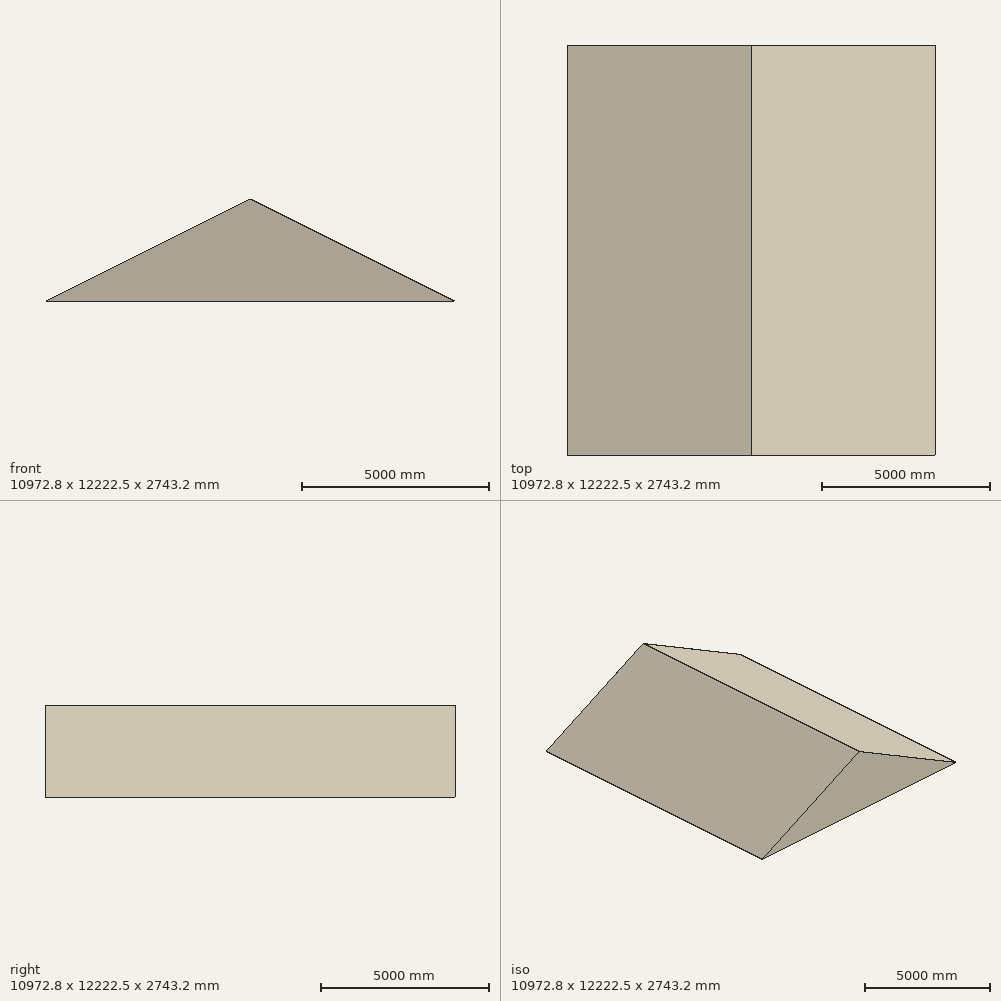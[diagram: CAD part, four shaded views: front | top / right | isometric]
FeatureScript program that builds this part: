
annotation { "Feature Type Name" : "Feature", "Feature Type Description" : "" }
export const myFeature = defineFeature(function(context is Context, id is Id, definition is map)
    precondition{}
    {
        {
            var Q0;
            Q0=qCreatedBy(makeId("Front.planeOp"),FACE);
            var sketch = newSketch(context, id + "F0", { "sketchPlane" : qUnion([Q0])});
            skLineSegment(sketch, "E0", {"start": v(0, 0) * mm, "end": v(-4572, 0) * mm});
            skLineSegment(sketch, "E1", {"start": v(0, 0) * mm, "end": v(4572, 0) * mm});
            skLineSegment(sketch, "E2", {"start": v(-4572, 0) * mm, "end": v(-4572, 3352.8) * mm});
            skLineSegment(sketch, "E3", {"start": v(4572, 0) * mm, "end": v(4572, 3352.8) * mm});
            skLineSegment(sketch, "E4", {"start": v(0, 0) * mm, "end": v(0, 3352.8) * mm, "construction": true});
            skLineSegment(sketch, "E5", {"start": v(4572, 3352.8) * mm, "end": v(0, 3352.8) * mm});
            skLineSegment(sketch, "E6", {"start": v(-4572, 3352.8) * mm, "end": v(0, 3352.8) * mm});
            skLineSegment(sketch, "E7", {"start": v(0, 3352.8) * mm, "end": v(0, 5638.8) * mm, "construction": true});
            skLineSegment(sketch, "E8", {"start": v(0, 5638.8) * mm, "end": v(4572, 3352.8) * mm});
            skLineSegment(sketch, "E9", {"start": v(0, 5638.8) * mm, "end": v(-4572, 3352.8) * mm});
            skLineSegment(sketch, "E10", {"start": v(4572, 3352.8) * mm, "end": v(5486.4, 3352.8) * mm});
            skLineSegment(sketch, "E11", {"start": v(-4572, 3352.8) * mm, "end": v(-5486.4, 3352.8) * mm});
            skLineSegment(sketch, "E12", {"start": v(0, 5638.8) * mm, "end": v(0, 6096) * mm});
            skLineSegment(sketch, "E13", {"start": v(0, 6096) * mm, "end": v(5486.4, 3352.8) * mm});
            skLineSegment(sketch, "E14", {"start": v(0, 6096) * mm, "end": v(-5486.4, 3352.8) * mm});
            skPoint(sketch, "E15.endSnap0", {"position": v(-5029.2, 3352.8) * mm});
            skLineSegment(sketch, "E16", {"start": v(-4572, 0) * mm, "end": v(-4572, -609.6) * mm});
            skLineSegment(sketch, "E17", {"start": v(-4572, -609.6) * mm, "end": v(4572, -609.6) * mm});
            skLineSegment(sketch, "E18", {"start": v(4572, 0) * mm, "end": v(4572, -609.6) * mm});
            skLineSegment(sketch, "E19", {"start": v(4572, 3352.8) * mm, "end": v(9143.16, 2743.2) * mm});
            skLineSegment(sketch, "E20", {"start": v(4572, 0) * mm, "end": v(9144, 0) * mm});
            skLineSegment(sketch, "E21", {"start": v(9144, 0) * mm, "end": v(9143.16, 2743.2) * mm});
            skLineSegment(sketch, "E22.bottom", {"start": v(609.6, 1981.2) * mm, "end": v(3352.8, 1981.2) * mm});
            skLineSegment(sketch, "E22.top", {"start": v(609.6, 609.6) * mm, "end": v(3352.8, 609.6) * mm});
            skLineSegment(sketch, "E22.left", {"start": v(609.6, 1981.2) * mm, "end": v(609.6, 609.6) * mm});
            skLineSegment(sketch, "E22.right", {"start": v(3352.8, 1981.2) * mm, "end": v(3352.8, 609.6) * mm});
            skLineSegment(sketch, "E23", {"start": v(4572, -609.6) * mm, "end": v(9144, -609.6) * mm});
            skLineSegment(sketch, "E24", {"start": v(9144, 0) * mm, "end": v(9144, -609.6) * mm});
            skLineSegment(sketch, "E25.0", {"start": v(762, 1828.8) * mm, "end": v(3200.4, 1828.8) * mm});
            skLineSegment(sketch, "E25.1", {"start": v(762, 1828.8) * mm, "end": v(762, 762) * mm});
            skLineSegment(sketch, "E25.2", {"start": v(762, 762) * mm, "end": v(3200.4, 762) * mm});
            skLineSegment(sketch, "E25.3", {"start": v(3200.4, 1828.8) * mm, "end": v(3200.4, 762) * mm});
            skLineSegment(sketch, "E26.bottom", {"start": v(7315.2, 609.6) * mm, "end": v(6096, 609.6) * mm});
            skLineSegment(sketch, "E26.top", {"start": v(7315.2, 1981.2) * mm, "end": v(6096, 1981.2) * mm});
            skLineSegment(sketch, "E26.left", {"start": v(7315.2, 609.6) * mm, "end": v(7315.2, 1981.2) * mm});
            skLineSegment(sketch, "E26.right", {"start": v(6096, 609.6) * mm, "end": v(6096, 1981.2) * mm});
            skLineSegment(sketch, "E27.0", {"start": v(6248.4, 762) * mm, "end": v(6248.4, 1828.8) * mm});
            skLineSegment(sketch, "E27.1", {"start": v(7162.8, 762) * mm, "end": v(6248.4, 762) * mm});
            skLineSegment(sketch, "E27.2", {"start": v(7162.8, 762) * mm, "end": v(7162.8, 1828.8) * mm});
            skLineSegment(sketch, "E27.3", {"start": v(7162.8, 1828.8) * mm, "end": v(6248.4, 1828.8) * mm});
            skLineSegment(sketch, "E28.bottom", {"start": v(-2438.4, 0) * mm, "end": v(-3352.8, 0) * mm});
            skLineSegment(sketch, "E28.top", {"start": v(-2438.4, 2133.6) * mm, "end": v(-3352.8, 2133.6) * mm});
            skLineSegment(sketch, "E28.left", {"start": v(-2438.4, 0) * mm, "end": v(-2438.4, 2133.6) * mm});
            skLineSegment(sketch, "E28.right", {"start": v(-3352.8, 0) * mm, "end": v(-3352.8, 2133.6) * mm});
            skLineSegment(sketch, "E29", {"start": v(4572, 2743.2) * mm, "end": v(9143.34, 2133.57) * mm});
            skLineSegment(sketch, "E30.bottom", {"start": v(-3200.4, 1981.2) * mm, "end": v(-2590.8, 1981.2) * mm});
            skLineSegment(sketch, "E30.top", {"start": v(-3200.4, 0) * mm, "end": v(-2590.8, 0) * mm});
            skLineSegment(sketch, "E30.left", {"start": v(-3200.4, 1981.2) * mm, "end": v(-3200.4, 0) * mm});
            skLineSegment(sketch, "E30.right", {"start": v(-2590.8, 1981.2) * mm, "end": v(-2590.8, 0) * mm});
            skSolve(sketch);
        }
        {
            var Q0;
            Q0=makeQuery(id+"F0.imprint","IMPRINT",FACE,{"disambiguationData":[TD([[makeQuery(id+"F0.imprint","IMPRINT",EDGE,{"derivedFrom":sQuery(id+"F0.wireOp",EDGE,"E9")}),-1.0]])]});
            var Q1;
            Q1=makeQuery(id+"F0.imprint","IMPRINT",FACE,{"disambiguationData":[TD([[makeQuery(id+"F0.imprint","IMPRINT",EDGE,{"derivedFrom":sQuery(id+"F0.wireOp",EDGE,"E8")}),1.0]])]});
            extrude(context, id + "F1", {"entities" : qUnion([Q0, Q1]), "depth" : 30.48 * mm, "offsetDistance" : 30.48 * mm, "hasSecondDirection" : true, "secondDirectionOppositeDirection" : true, "secondDirectionDepth" : 12192 * mm});
        }
        {
            var Q0;
            Q0=makeQuery(id+"F0.imprint","IMPRINT",FACE,{"disambiguationData":[TD([[makeQuery(id+"F0.imprint","IMPRINT",EDGE,{"derivedFrom":sQuery(id+"F0.wireOp",EDGE,"E5")}),-1.0]])]});
            extrude(context, id + "F2", {"entities" : qUnion([Q0]), "operationType" : NewBodyOperationType.ADD, "depth" : 30.48 * mm, "offsetDistance" : 30.48 * mm, "hasSecondDirection" : true, "secondDirectionOppositeDirection" : true, "secondDirectionDepth" : 12192 * mm});
        }
    });
